# Revit family: Soccer-Goal_Shootout-Portable-Square
name_source: partatom
category: Generic Models
units: mm (PartAtom-declared; Revit-internal decimal feet)

## family parameters
Always vertical = Yes
Can host rebar = No
Classification Number = 23.40.50.34.14
Cut with Voids When Loaded = No
Maintain Annotation Orientation = No
Part Type = Normal
Room Calculation Point = No
Round Connector Dimension = Use Diameter
Shared = No
Work Plane-Based = No

## types (6) — shared parameters
Ballasts = Ballasts - Sandbag
Building Codes = https://www.brpbybison.com
Construction Details = https://www.arcat.com
Default Elevation = 0' - 0"
Description = IPI by Bison Gymnasium Equipment
Frame Material = Aluminum
Green Building-LEED = https://www.arcat.com
Installation-Fabrication = http://www.ipibybison.com
Keynote = 11 66 00
Manufacturer = BRP by bison
Manufacturer Fax = 888-438-5312
Manufacturer Website = http://www.ipibybison.com
Model = As Specified
Netting = Finish - IPI by Bison - White Netting
Product Data = http://www.arcat.com
Revision = R1_2018-09
Sales Information = http://www.ipibybison.com
Specification = https://www.arcat.com
Square Frame Color = Powder Coat - White
Test Data = http://www.ipibybison.com
Top Depth = 4' - 0"
URL = https://ipibybison.com

## per-type parameters (varying)
| type | Ballasted | Base Depth | Goal Clearance | Height |
| SC1865PA44E - Anchored | No | 6' - 6" | 18' - 6" | 6' - 6" |
| SC2480PA44E - Anchored | No | 10' - 0" | 24' - 0" | 8' - 0" |
| SC1865PA44NT - Ballasted | Yes | 6' - 6" | 18' - 6" | 6' - 6" |
| SC2170PA44NT - Ballasted | Yes | 7' - 0" | 21' - 0" | 7' - 0" |
| SC2170PA44E - Anchored | No | 7' - 0" | 21' - 0" | 7' - 0" |
| SC2480PA44NT - Ballasted | Yes | 10' - 0" | 24' - 0" | 8' - 0" |

## geometry (parser evidence)
native form markers: Blend x4, Sweep x3
no freeform markers — native parametric forms only
